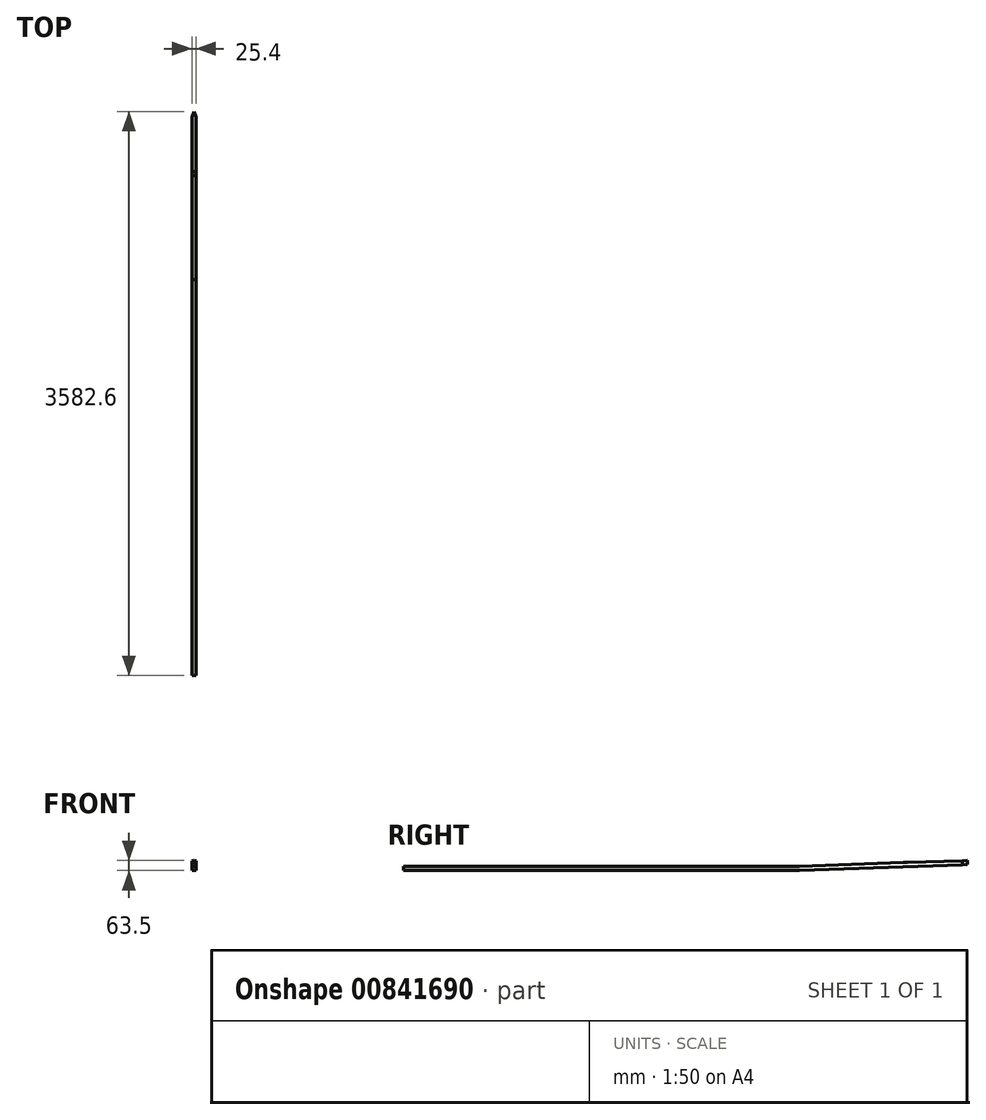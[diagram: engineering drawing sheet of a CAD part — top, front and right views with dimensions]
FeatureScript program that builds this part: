
annotation { "Feature Type Name" : "Feature", "Feature Type Description" : "" }
export const myFeature = defineFeature(function(context is Context, id is Id, definition is map)
    precondition{}
    {
        {
            var Q0;
            Q0=qCreatedBy(makeId("Top.planeOp"),FACE);
            var sketch = newSketch(context, id + "F0", { "sketchPlane" : qUnion([Q0])});
            skLineSegment(sketch, "E0", {"start": v(0, 1791.3) * mm, "end": v(0, -1791.3) * mm, "construction": true});
            skLineSegment(sketch, "E1", {"start": v(0, 0) * mm, "end": v(-381, 0) * mm, "construction": true});
            skLineSegment(sketch, "E2", {"start": v(0, -1791.3) * mm, "end": v(-228.6, -1791.3) * mm, "construction": true});
            skArc(sketch, "E3", {"start": v(0, 1791.3) * mm, "mid": v(-379.94, 16.95) * mm, "end": v(-228.6, -1791.3) * mm, "construction": true});
            skLineSegment(sketch, "E4", {"start": v(0, -1791.3) * mm, "end": v(-12.7, -1791.3) * mm});
            skLineSegment(sketch, "E5", {"start": v(-12.7, -1791.3) * mm, "end": v(-12.7, 1757.06) * mm});
            skLineSegment(sketch, "E6", {"start": v(-12.7, 1757.06) * mm, "end": v(0, 1791.3) * mm});
            skLineSegment(sketch, "E7.MirrorCS", {"start": v(12.7, 1757.06) * mm, "end": v(0, 1791.3) * mm});
            skLineSegment(sketch, "E8.MirrorCS", {"start": v(12.7, -1791.3) * mm, "end": v(12.7, 1757.06) * mm});
            skLineSegment(sketch, "E9", {"start": v(0, -1791.3) * mm, "end": v(12.7, -1791.3) * mm});
            skSolve(sketch);
        }
        {
            var Q0;
            Q0 = qSketchRegion(id + "F0", true);
            extrude(context, id + "F1", {"entities" : qUnion([Q0]), "depth" : 63.5 * mm, "offsetDistance" : 25.4 * mm});
        }
        {
            var Q0;
            Q0=makeQuery(id+"F1.opExtrude","SWEPT_FACE",FACE,{"disambiguationData":[OSD([sQuery(id+"F0.wireOp",EDGE,"E8.MirrorCS")])]});
            var sketch = newSketch(context, id + "F2", { "sketchPlane" : qUnion([Q0])});
            skLineSegment(sketch, "E10", {"start": v(-1791.3, 63.5) * mm, "end": v(-1791.3, 25.4) * mm});
            skLineSegment(sketch, "E11", {"start": v(-1791.3, 25.4) * mm, "end": v(723.3, 25.4) * mm});
            skLineSegment(sketch, "E12", {"start": v(1791.3, 63.5) * mm, "end": v(1791.3, 38.1) * mm, "construction": true});
            skLineSegment(sketch, "E13", {"start": v(-1791.3, 63.5) * mm, "end": v(1791.3, 63.5) * mm});
            skLineSegment(sketch, "E14", {"start": v(1383.7, 50.8) * mm, "end": v(1409.1, 50.8) * mm});
            skLineSegment(sketch, "E15", {"start": v(723.3, 25.4) * mm, "end": v(1383.7, 50.8) * mm});
            skLineSegment(sketch, "E16", {"start": v(723.3, 25.4) * mm, "end": v(723.3, 0) * mm, "construction": true});
            skLineSegment(sketch, "E17", {"start": v(723.3, 0) * mm, "end": v(1791.3, 38.1) * mm});
            skLineSegment(sketch, "E18", {"start": v(1409.1, 50.8) * mm, "end": v(1791.3, 63.5) * mm});
            skLineSegment(sketch, "E19", {"start": v(723.3, 0) * mm, "end": v(1791.3, 0) * mm});
            skLineSegment(sketch, "E20", {"start": v(1791.3, 0) * mm, "end": v(1791.3, 38.1) * mm});
            skSolve(sketch);
        }
        {
            var Q0;
            Q0 = qSketchRegion(id + "F2", true);
            extrude(context, id + "F3", {"entities" : qUnion([Q0]), "operationType" : NewBodyOperationType.REMOVE, "oppositeDirection" : true, "depth" : 25.4 * mm, "offsetDistance" : 25.4 * mm});
        }
    });
